# Revit family: CENTUM Profil XL 200 WST 8m
name_source: partatom
category: HLS-Bauteile
revit_build: Autodesk Revit 2017 (Build: 20190507_1515(x64)
units: mm (PartAtom-declared; Revit-internal decimal feet)

## family parameters
Arbeitsebenenbasiert = Ja
Beim Laden mit Abzugskörper schneiden = Nein
Bemaßung runder Anschluss = Durchmesser verwenden
Gemeinsam genutzt = Ja
Immer vertikal = Nein
Raumberechnungspunkt = Nein
Teiletyp = Normal

## types (1)
- CENTUM Profil XL200 WST L=8000
    Abmessung = 100/200/5.0 mm
    Artikelnummer = 16020080
    Breite = 100 mm  [stored 0.328084 ft]
    Bund = 32 m
    EAN = 4250928449405
    Fabrikat = MEFA
    Firma = MEFA Befestigungs- und Montagesysteme GmbH
    Fläche (schwächster Profilquerschnitt) = 0 m²
    Gewicht = 20,46 kg
    Höhe = 200 mm
    Kurztext1 = Montageprofil CENTUM XL 200 WST
    Kurztext2 = 100 / 200 / 5 mm L= 8 m fsv
    Langloch = 14.0 x 65.0 mm
    Länge = 8000 mm  [stored 26.2467 ft]
    Material = Stahl
    Materialname = S275
    Mengeneinheit = m
    Oberflaeche = feuerstückverzinkt
    Streckgrenze = 275 N/mm²
    Stärke = 5 mm  [stored 0.0164042 ft]
    Torsionswiderstandsmoment Wt = 185,25 cm³
    Trägheitsradius iy = 7,21 cm
    Trägheitsradius iz = 4,24 cm
    Vorgabe-Ansicht = 1219 mm
    Widerstandsmoment Wy = 125,56 cm³
    Widerstandsmoment Wz = 86,69 cm³
    vpe = 8 m

note: [stored X ft] marks values corroborated as IEEE doubles in the binary element streams (Revit-internal decimal feet)
